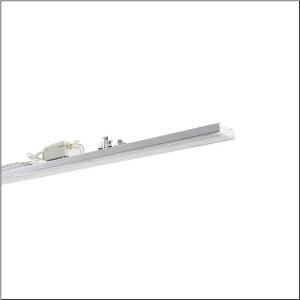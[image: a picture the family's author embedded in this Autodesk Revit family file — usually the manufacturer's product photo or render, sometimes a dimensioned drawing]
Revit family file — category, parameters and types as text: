
# Revit family: licross_r__21_recessed_mo_52tl10dv4e5g_ca6c
name_source: partatom
category: Lighting Fixtures
units: mm (PartAtom-declared; Revit-internal decimal feet)

## family parameters
Cut with Voids When Loaded = No
Host = Face
Light Source = No
Part Type = Normal
Room Calculation Point = No
Round Connector Dimension = Use Diameter
Shared = No

## types (1)
- --- (1 x LED, 14990 lm, 85.3 W, 4000K)
    Apparent Load = 85 VA
    CIE Flux Codes = 50 81 96 100 100
    Color Rendering = 80
    Color Temperature = 4000K
    Default Elevation = 1800 mm
    Description = Licross® 21 Recessed MO, luminaire insert, of sheet steel, galvanised, coil coated, white, length: 2.250mm, width: 66mm, height: 67mm, LED rated luminous flux: 14.990lm, light colour: 840, control gear: DALI 2, with plug, 5-pole, with phase selection, mains connection: 220..240V, AC, 50/60Hz, rated input power: 85W, halogen-free wiring, primary optical cover: cover, of PMMA, light emission: direct distribution, primary light characteristic: symmetric, protection rating (complete): IP40, insulation class (complete): insulation class I (protective earthing), certification: CE, ENEC, VDE, UKCA, protection symbol: D if used in an environment without relevant dust loads with corresponding accessories, impact resistance: IK06, permissible ambient temperature for indoor applications: -25..+35°C, corresponds to IFS (International Featured Standards) requirements for safety and quality in the food industry, reducing of maximum allowable ambient temperature of 5°C with ceiling mounting, LABS conformity tested according to VDMA 24364:2018-05, packaging unit: 1 piece
    Height = 58 mm
    Lamp = 1 x LED
    Lamp Light Flux = 14990 lm
    Lamp Power = 85.3 W
    Lamp count = 1
    Length = 2250 mm
    Luminous efficacy = 176 lm/W
    Manufacturer = Siteco
    ModVariant = No
    Model = 52TL10DV4E5G
    Mounting Place = Ceiling
    Mounting Type = Pendant
    Number of Poles = 1
    OnlyDefault = Yes
    Power Factor = 1
    Product Name = Licross® 21 Recessed MO
    Product group = luminaire insert
    ProductGroupID = 901
    Protection Class = Protection class I
    Protection Degree = IP 40
    RLX_Detail_Level = 1
    RLX_Emergency_Light_Flux = 0 lm
    RLX_Emergency_Type = 0
    RLX_Emergency_Type_DB = No
    RlxData = <blob elided: 29201 chars, md5=3cb31432>
    Socket = socket
    Standby Power = 0 W
    System Light Flux = 14990 lm
    System Power = 85 W
    Type Comments = factory setting: luminous flux: 100 % | dim-lin: 254 | 390 mA
    Type Image = l_1296930.jpg
    URL = http://relux.com
    VarID = @adj_059245
    Voltage = 0 V
    Weight = 0.00 kg
    Width = 66 mm

## geometry (parser evidence)
native form markers: Blend x4, Sweep x10
no freeform markers — native parametric forms only
